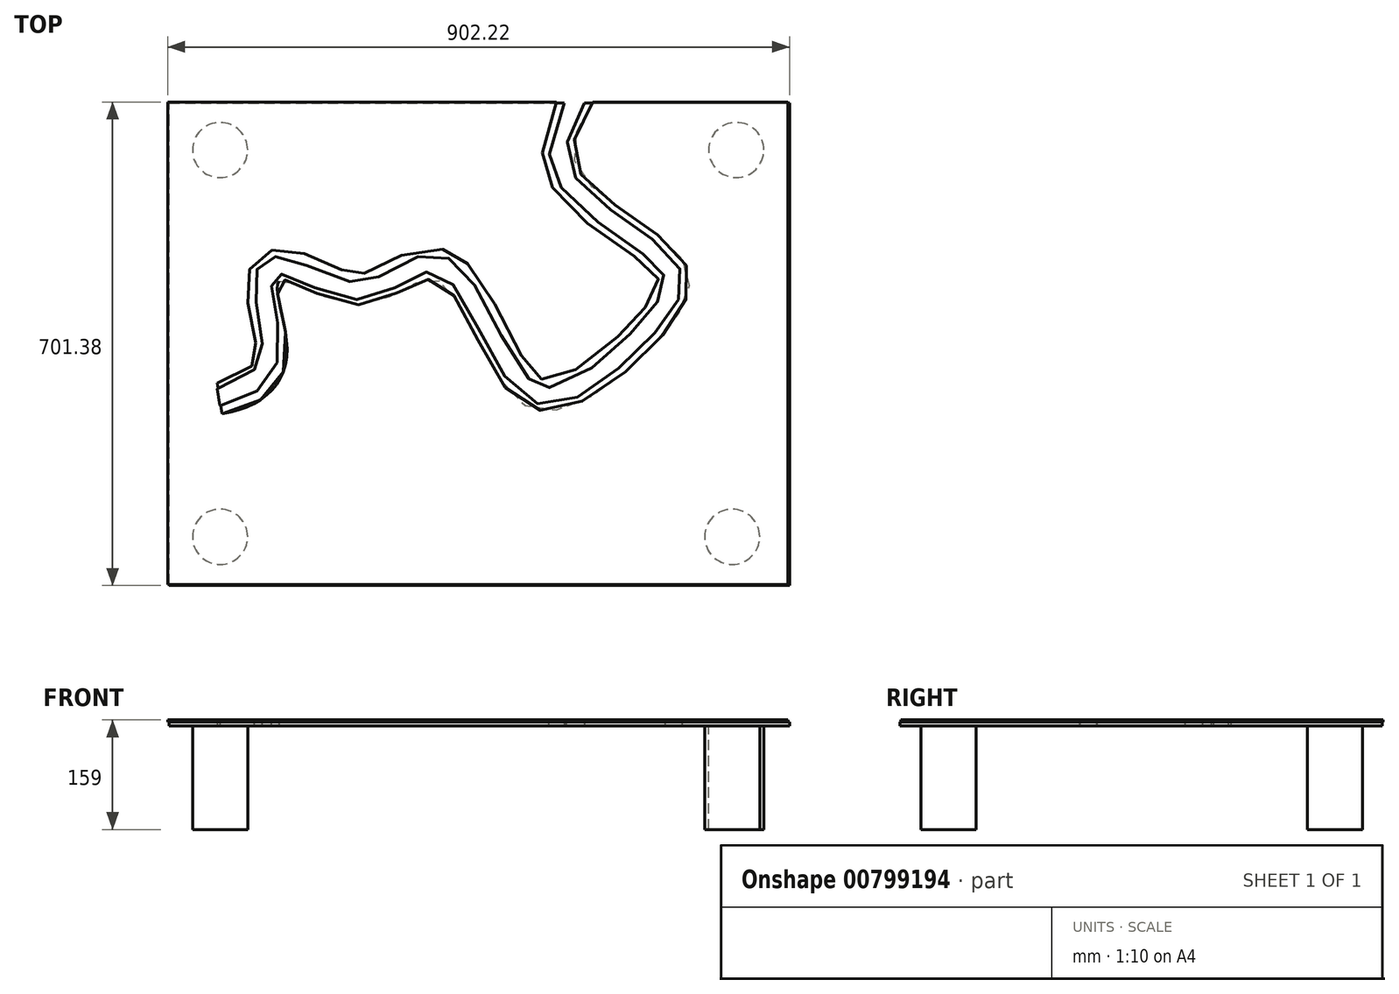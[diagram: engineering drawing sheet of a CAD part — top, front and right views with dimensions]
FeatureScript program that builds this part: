
annotation { "Feature Type Name" : "Feature", "Feature Type Description" : "" }
export const myFeature = defineFeature(function(context is Context, id is Id, definition is map)
    precondition{}
    {
        {
            var Q0;
            Q0=qCreatedBy(makeId("Top.planeOp"),FACE);
            var sketch = newSketch(context, id + "F0", { "sketchPlane" : qUnion([Q0])});
            skLineSegment(sketch, "E0.bottom", {"start": v(-313.22, -209.62) * mm, "end": v(586.78, -209.62) * mm});
            skLineSegment(sketch, "E0.top", {"start": v(-313.22, 490.38) * mm, "end": v(586.78, 490.38) * mm});
            skLineSegment(sketch, "E0.left", {"start": v(-313.22, -209.62) * mm, "end": v(-313.22, 490.38) * mm});
            skLineSegment(sketch, "E0.right", {"start": v(586.78, -209.62) * mm, "end": v(586.78, 490.38) * mm});
            skSolve(sketch);
        }
        {
            var Q0;
            Q0=qCreatedBy(makeId("Top.planeOp"),FACE);
            var sketch = newSketch(context, id + "F1", { "sketchPlane" : qUnion([Q0])});
            skFitSpline(sketch, "E1", {"points": [v(-234.3, 37.79) * mm, v(-140.37, 121) * mm, v(-151.1, 231.03) * mm, v(-33, 196.14) * mm, v(79.72, 231.03) * mm, v(203.18, 51.2) * mm, v(383, 129.04) * mm, v(436.68, 257.87) * mm, v(281.01, 394.76) * mm, v(345.43, 545.06) * mm], "startDerivative": vector(1524.68, 246.4) * mm, "endDerivative": vector(1140, 1409.82) * mm});
            skFitSpline(sketch, "E2.0", {"points": [v(-241.49, 82.21) * mm, v(-235.54, 83.17) * mm, v(-227.18, 85.14) * mm, v(-217.47, 88.6) * mm, v(-210.97, 91.54) * mm, v(-205.27, 94.74) * mm, v(-200.42, 98.12) * mm, v(-196.37, 101.6) * mm, v(-193.1, 105.12) * mm, v(-190.48, 108.67) * mm, v(-188.77, 111.71) * mm, v(-187.64, 114.26) * mm, v(-186.91, 116.25) * mm, v(-186.29, 118.34) * mm, v(-185.86, 120.2) * mm, v(-185.58, 121.76) * mm, v(-185.4, 122.98) * mm, v(-185.25, 124.24) * mm, v(-185.14, 125.55) * mm, v(-185.06, 127) * mm, v(-185, 129.09) * mm, v(-185.02, 131.99) * mm, v(-185.23, 135.87) * mm, v(-185.6, 140.08) * mm, v(-186.16, 144.57) * mm, v(-187.1, 150.85) * mm, v(-188.62, 159.15) * mm, v(-190.82, 169.5) * mm, v(-192.8, 178.27) * mm, v(-194.38, 185.3) * mm, v(-195.53, 190.6) * mm, v(-196.61, 195.94) * mm, v(-197.6, 201.35) * mm, v(-198.47, 206.9) * mm, v(-199.15, 212.74) * mm, v(-199.48, 218.02) * mm, v(-199.49, 222.66) * mm, v(-199.33, 226.42) * mm, v(-198.92, 230.53) * mm, v(-198.17, 235.06) * mm, v(-196.91, 240.08) * mm, v(-194.95, 245.63) * mm, v(-192.49, 250.64) * mm, v(-189.9, 254.77) * mm, v(-187.62, 257.88) * mm, v(-185, 260.93) * mm, v(-182.04, 263.87) * mm, v(-179.31, 266.15) * mm, v(-177, 267.85) * mm, v(-174.62, 269.45) * mm, v(-171.6, 271.2) * mm, v(-167.98, 272.95) * mm, v(-164.4, 274.33) * mm, v(-159.8, 275.75) * mm, v(-154.43, 276.82) * mm, v(-148.71, 277.31) * mm, v(-143.68, 277.28) * mm, v(-139.23, 276.9) * mm, v(-135.25, 276.33) * mm, v(-131.65, 275.6) * mm, v(-128.33, 274.8) * mm, v(-124.2, 273.62) * mm, v(-119.45, 272.03) * mm, v(-114.13, 270) * mm, v(-109.02, 267.87) * mm, v(-104, 265.67) * mm, v(-99.04, 263.41) * mm, v(-94.1, 261.12) * mm, v(-87.5, 258.07) * mm, v(-79.29, 254.3) * mm, v(-69.56, 250.1) * mm, v(-61.74, 247.1) * mm, v(-55.8, 245.08) * mm, v(-51.55, 243.8) * mm, v(-47.55, 242.76) * mm, v(-43.86, 241.98) * mm, v(-41.09, 241.53) * mm, v(-39.08, 241.3) * mm, v(-37.68, 241.18) * mm, v(-36.4, 241.12) * mm, v(-35.42, 241.1) * mm, v(-34.7, 241.11) * mm, v(-34.2, 241.13) * mm, v(-33.69, 241.15) * mm, v(-32.98, 241.2) * mm, v(-32.08, 241.3) * mm, v(-30.94, 241.45) * mm, v(-29.75, 241.65) * mm, v(-28.07, 242) * mm, v(-25.82, 242.56) * mm, v(-21.88, 243.8) * mm, v(-16.33, 245.98) * mm, v(-8.81, 249.56) * mm, v(-0.54, 253.95) * mm, v(8.45, 258.93) * mm, v(16.64, 263.34) * mm, v(23.76, 266.88) * mm, v(29.45, 269.5) * mm, v(35.56, 272) * mm, v(42.18, 274.31) * mm, v(49.42, 276.3) * mm, v(57.37, 277.8) * mm, v(66.05, 278.55) * mm, v(75.38, 278.28) * mm, v(83.51, 276.98) * mm, v(89.2, 275.43) * mm, v(92.44, 274.37) * mm, v(94.84, 273.49) * mm, v(96.82, 272.68) * mm, v(98.38, 271.98) * mm, v(99.93, 271.27) * mm, v(101.8, 270.35) * mm, v(104.7, 268.8) * mm, v(108.13, 266.74) * mm, v(111.95, 264.14) * mm, v(115.5, 261.43) * mm, v(119.93, 257.72) * mm, v(124.92, 252.93) * mm, v(130.25, 247.03) * mm, v(135.09, 241) * mm, v(139.55, 234.84) * mm, v(145.13, 226.49) * mm, v(151.56, 215.76) * mm, v(158.77, 202.5) * mm, v(165.68, 188.95) * mm, v(172.42, 175.3) * mm, v(179.06, 161.74) * mm, v(185.66, 148.52) * mm, v(192.24, 135.9) * mm, v(198.8, 124.17) * mm, v(205.28, 113.64) * mm, v(210.51, 106.14) * mm, v(214.49, 101.06) * mm, v(217.33, 97.75) * mm, v(219.98, 94.97) * mm, v(222.38, 92.74) * mm, v(224.11, 91.33) * mm, v(225.31, 90.46) * mm, v(226.12, 89.92) * mm, v(226.8, 89.5) * mm, v(227.47, 89.14) * mm, v(228.13, 88.82) * mm, v(229, 88.44) * mm, v(230.1, 88.05) * mm, v(231.55, 87.67) * mm, v(233.18, 87.38) * mm, v(235.06, 87.2) * mm, v(237.23, 87.16) * mm, v(240.56, 87.34) * mm, v(245.52, 88.08) * mm, v(252.68, 90) * mm, v(260.83, 93.03) * mm, v(269.76, 97.18) * mm, v(279.26, 102.4) * mm, v(289.15, 108.58) * mm, v(299.28, 115.62) * mm, v(309.5, 123.37) * mm, v(319.73, 131.71) * mm, v(329.83, 140.5) * mm, v(338.06, 148.1) * mm, v(344.5, 154.26) * mm, v(348.45, 158.13) * mm, v(351.56, 161.24) * mm, v(354.63, 164.33) * mm, v(358.35, 168.16) * mm, v(362.65, 172.7) * mm, v(368.12, 178.65) * mm, v(374.44, 185.9) * mm, v(381.12, 194.2) * mm, v(386.79, 202.03) * mm, v(391.37, 209.25) * mm, v(394.83, 215.7) * mm, v(397.17, 221.22) * mm, v(398.27, 224.9) * mm, v(398.76, 227.25) * mm, v(398.96, 228.73) * mm, v(399.03, 229.95) * mm, v(399.02, 230.95) * mm, v(398.94, 231.79) * mm, v(398.8, 232.54) * mm, v(398.6, 233.28) * mm, v(398.36, 233.97) * mm, v(398.1, 234.6) * mm, v(397.89, 235.03) * mm, v(397.7, 235.4) * mm, v(397.54, 235.68) * mm, v(397.36, 236) * mm, v(397.09, 236.45) * mm, v(396.68, 237.09) * mm, v(395.87, 238.27) * mm, v(394.57, 240) * mm, v(392.51, 242.4) * mm, v(389.14, 246) * mm, v(383.77, 251.06) * mm, v(375.75, 257.74) * mm, v(366.42, 264.84) * mm, v(356.04, 272.25) * mm, v(344.87, 279.92) * mm, v(333.15, 287.84) * mm, v(321.1, 296.03) * mm, v(308.9, 304.53) * mm, v(296.74, 313.4) * mm, v(284.8, 322.77) * mm, v(273.24, 332.8) * mm, v(264.04, 341.9) * mm, v(257.06, 349.83) * mm, v(252.04, 356.16) * mm, v(248.1, 361.8) * mm, v(245.13, 366.57) * mm, v(243, 370.28) * mm, v(241.31, 373.49) * mm, v(240.03, 376.13) * mm, v(238.81, 378.8) * mm, v(237.4, 382.16) * mm, v(235.37, 387.62) * mm, v(233.3, 394.55) * mm, v(231.55, 402.95) * mm, v(230.52, 411.32) * mm, v(230.17, 419.6) * mm, v(230.45, 427.73) * mm, v(231.56, 438.3) * mm, v(234.19, 450.95) * mm, v(238.83, 465.24) * mm, v(244.61, 478.77) * mm, v(251.28, 491.68) * mm, v(258.65, 504.13) * mm, v(266.58, 516.22) * mm, v(274.94, 528.03) * mm, v(283.61, 539.62) * mm, v(295.46, 554.84) * mm, v(304.5, 566) * mm, v(310.44, 573.35) * mm]});
            skLineSegment(sketch, "E3", {"start": v(-241.49, 82.21) * mm, "end": v(-234.3, 37.79) * mm});
            skLineSegment(sketch, "E4", {"start": v(345.43, 545.06) * mm, "end": v(310.44, 573.35) * mm});
            skSolve(sketch);
        }
        {
            var Q0;
            Q0=qSketchRegion(id+"F0",true);
            extrude(context, id + "F2", {"entities" : qUnion([Q0]), "depth" : 3 * mm, "offsetDistance" : 25 * mm});
        }
        {
            var Q0;
            Q0=qSketchRegion(id+"F1",true);
            extrude(context, id + "F3", {"entities" : qUnion([Q0]), "operationType" : NewBodyOperationType.REMOVE, "depth" : 25 * mm, "offsetDistance" : 25 * mm, "hasSecondDirection" : true, "secondDirectionOppositeDirection" : true, "secondDirectionDepth" : 25 * mm});
        }
        {
            var Q0;
            Q0=qCreatedBy(makeId("Top.planeOp"),FACE);
            var sketch = newSketch(context, id + "F4", { "sketchPlane" : qUnion([Q0])});
            skFitSpline(sketch, "E5", {"points": [v(-329.28, -233.28) * mm, v(-243.32, -152.04) * mm, v(-250.13, -43.12) * mm, v(-125.32, -79.42) * mm, v(-10.38, -40.77) * mm, v(117.48, -224.65) * mm, v(288.03, -142.03) * mm, v(335.32, -29.5) * mm, v(179.23, 110.07) * mm, v(250.45, 273.99) * mm], "startDerivative": vector(1524.68, 246.4) * mm, "endDerivative": vector(1140, 1409.82) * mm});
            skFitSpline(sketch, "E6.0", {"points": [v(-333.27, -208.6) * mm, v(-326.54, -207.51) * mm, v(-317.2, -205.24) * mm, v(-306.38, -201.13) * mm, v(-299.12, -197.57) * mm, v(-292.69, -193.58) * mm, v(-287.08, -189.2) * mm, v(-282.25, -184.47) * mm, v(-278.16, -179.38) * mm, v(-274.75, -173.88) * mm, v(-272, -167.9) * mm, v(-270.26, -162.45) * mm, v(-269.35, -158.34) * mm, v(-268.92, -155.91) * mm, v(-268.64, -154.04) * mm, v(-268.42, -152.13) * mm, v(-268.27, -150.5) * mm, v(-268.18, -149.16) * mm, v(-268.1, -147.79) * mm, v(-268.04, -146.03) * mm, v(-268, -143.84) * mm, v(-268.03, -140.83) * mm, v(-268.18, -136.9) * mm, v(-268.54, -131.97) * mm, v(-269.24, -125.18) * mm, v(-270.46, -116.36) * mm, v(-272.3, -105.55) * mm, v(-274.33, -94.74) * mm, v(-276.32, -84.13) * mm, v(-277.77, -75.54) * mm, v(-278.7, -68.8) * mm, v(-279.22, -63.78) * mm, v(-279.54, -58.73) * mm, v(-279.56, -53.56) * mm, v(-279.23, -49.02) * mm, v(-278.6, -45.13) * mm, v(-277.9, -42.06) * mm, v(-276.88, -38.81) * mm, v(-275.45, -35.39) * mm, v(-273.48, -31.84) * mm, v(-271.3, -28.87) * mm, v(-269.22, -26.58) * mm, v(-267.5, -24.94) * mm, v(-265.93, -23.67) * mm, v(-264.6, -22.72) * mm, v(-263.58, -22.04) * mm, v(-262.54, -21.4) * mm, v(-261.14, -20.62) * mm, v(-259.37, -19.76) * mm, v(-257.27, -18.92) * mm, v(-254.5, -18.02) * mm, v(-251.2, -17.3) * mm, v(-247.53, -16.9) * mm, v(-244.15, -16.83) * mm, v(-241.02, -17) * mm, v(-238.1, -17.36) * mm, v(-234.43, -18) * mm, v(-230.15, -19.07) * mm, v(-225.24, -20.6) * mm, v(-220.43, -22.37) * mm, v(-215.62, -24.3) * mm, v(-209.16, -27.07) * mm, v(-200.92, -30.82) * mm, v(-190.7, -35.56) * mm, v(-180.25, -40.28) * mm, v(-169.7, -44.71) * mm, v(-159.26, -48.6) * mm, v(-150.83, -51.16) * mm, v(-144.4, -52.7) * mm, v(-139.76, -53.6) * mm, v(-135.35, -54.2) * mm, v(-131.9, -54.46) * mm, v(-129.28, -54.53) * mm, v(-127.39, -54.5) * mm, v(-125.58, -54.4) * mm, v(-123.76, -54.24) * mm, v(-121.92, -54) * mm, v(-119.44, -53.6) * mm, v(-115.02, -52.63) * mm, v(-108.46, -50.55) * mm, v(-100.2, -47.01) * mm, v(-91.65, -42.63) * mm, v(-82.84, -37.63) * mm, v(-73.78, -32.3) * mm, v(-64.42, -26.92) * mm, v(-56.22, -22.65) * mm, v(-49.28, -19.55) * mm, v(-43.81, -17.45) * mm, v(-38.04, -15.66) * mm, v(-31.91, -14.28) * mm, v(-25.39, -13.48) * mm, v(-18.5, -13.42) * mm, v(-12.56, -14.13) * mm, v(-7.79, -15.23) * mm, v(-4.82, -16.13) * mm, v(-2.48, -16.98) * mm, v(-0.74, -17.69) * mm, v(0.97, -18.46) * mm, v(3.19, -19.54) * mm, v(5.85, -21.01) * mm, v(9.87, -23.56) * mm, v(14.5, -27.07) * mm, v(19.54, -31.66) * mm, v(24.17, -36.56) * mm, v(28.5, -41.75) * mm, v(32.61, -47.19) * mm, v(37.85, -54.76) * mm, v(44.07, -64.8) * mm, v(51.22, -77.59) * mm, v(58.2, -90.95) * mm, v(65.1, -104.67) * mm, v(71.98, -118.53) * mm, v(78.9, -132.26) * mm, v(85.86, -145.61) * mm, v(92.9, -158.3) * mm, v(100, -170.04) * mm, v(107.11, -180.53) * mm, v(112.99, -187.97) * mm, v(117.56, -193) * mm, v(120.9, -196.27) * mm, v(123.56, -198.58) * mm, v(125.61, -200.17) * mm, v(127.1, -201.23) * mm, v(128.3, -202.01) * mm, v(129.23, -202.58) * mm, v(130.14, -203.1) * mm, v(131.27, -203.7) * mm, v(132.63, -204.33) * mm, v(133.99, -204.9) * mm, v(135.82, -205.55) * mm, v(138.15, -206.2) * mm, v(141.08, -206.74) * mm, v(145.21, -207.13) * mm, v(150.9, -206.98) * mm, v(158.66, -205.64) * mm, v(167.24, -203.07) * mm, v(176.5, -199.26) * mm, v(186.27, -194.27) * mm, v(196.38, -188.2) * mm, v(206.71, -181.2) * mm, v(217.13, -173.38) * mm, v(227.54, -164.92) * mm, v(237.85, -155.95) * mm, v(247.97, -146.62) * mm, v(256.18, -138.68) * mm, v(262.58, -132.3) * mm, v(267.29, -127.51) * mm, v(271.9, -122.75) * mm, v(276.35, -118.06) * mm, v(280.64, -113.46) * mm, v(286.1, -107.43) * mm, v(292.45, -100.11) * mm, v(299.17, -91.72) * mm, v(304.9, -83.77) * mm, v(309.53, -76.35) * mm, v(313.03, -69.56) * mm, v(315.38, -63.52) * mm, v(316.45, -59.18) * mm, v(316.87, -56.11) * mm, v(316.98, -53.98) * mm, v(316.92, -51.98) * mm, v(316.69, -50.07) * mm, v(316.28, -48.17) * mm, v(315.78, -46.54) * mm, v(315.25, -45.2) * mm, v(314.8, -44.15) * mm, v(314.35, -43.25) * mm, v(313.96, -42.51) * mm, v(313.64, -41.95) * mm, v(313.3, -41.37) * mm, v(312.8, -40.57) * mm, v(312.12, -39.52) * mm, v(311.18, -38.19) * mm, v(309.78, -36.33) * mm, v(307.74, -33.87) * mm, v(304.84, -30.72) * mm, v(301.53, -27.42) * mm, v(296.58, -22.85) * mm, v(289.5, -16.9) * mm, v(279.83, -9.45) * mm, v(269.23, -1.78) * mm, v(257.93, 6.1) * mm, v(246.18, 14.16) * mm, v(234.19, 22.45) * mm, v(222.16, 30.97) * mm, v(210.3, 39.77) * mm, v(198.81, 48.92) * mm, v(187.87, 58.5) * mm, v(179.37, 66.95) * mm, v(173.05, 74.08) * mm, v(168.58, 79.64) * mm, v(164.41, 85.45) * mm, v(161.24, 90.51) * mm, v(158.9, 94.72) * mm, v(157.27, 97.96) * mm, v(155.76, 101.28) * mm, v(154.4, 104.64) * mm, v(153.17, 108.03) * mm, v(151.74, 112.58) * mm, v(149.76, 120.63) * mm, v(148.36, 132.2) * mm, v(148.77, 145.9) * mm, v(150.94, 159.27) * mm, v(154.56, 172.24) * mm, v(159.38, 184.86) * mm, v(165.2, 197.18) * mm, v(171.86, 209.28) * mm, v(181.66, 225.16) * mm, v(195.32, 244.62) * mm, v(213.03, 267.48) * mm, v(225.08, 282.37) * mm, v(231.01, 289.7) * mm]});
            skLineSegment(sketch, "E7", {"start": v(-333.27, -208.6) * mm, "end": v(-329.28, -233.28) * mm});
            skLineSegment(sketch, "E8", {"start": v(250.45, 273.99) * mm, "end": v(231.01, 289.7) * mm});
            skSolve(sketch);
        }
        {
            var Q0;
            Q0=makeQuery(id+"F2.opExtrude","SWEPT_BODY",BODY,{"disambiguationData":[OSD([sQuery(id+"F0.wireOp",EDGE,"E0.bottom"),sQuery(id+"F0.wireOp",EDGE,"E0.top"),sQuery(id+"F0.wireOp",EDGE,"E0.left"),sQuery(id+"F0.wireOp",EDGE,"E0.right")])]});
            transform(context, id + "F5", {"entities" : qUnion([Q0]), "transformType" : TransformType.TRANSLATION_3D, "dx" : -139 * mm, "dy" : -139 * mm, "dz" : 6 * mm, "makeCopy" : false});
        }
        {
            var Q0;
            Q0=qSketchRegion(id+"F4",true);
            extrude(context, id + "F6", {"entities" : qUnion([Q0]), "depth" : 25 * mm, "offsetDistance" : 25 * mm, "hasSecondDirection" : true, "secondDirectionOppositeDirection" : true, "secondDirectionDepth" : 25 * mm});
        }
        {
            var Q0;
            Q0=qCreatedBy(makeId("Top.planeOp"),FACE);
            var sketch = newSketch(context, id + "F7", { "sketchPlane" : qUnion([Q0])});
            skLineSegment(sketch, "E9.bottom", {"start": v(-450, -350) * mm, "end": v(450, -350) * mm});
            skLineSegment(sketch, "E9.top", {"start": v(-450, 350) * mm, "end": v(450, 350) * mm});
            skLineSegment(sketch, "E9.left", {"start": v(-450, -350) * mm, "end": v(-450, 350) * mm});
            skLineSegment(sketch, "E9.right", {"start": v(450, -350) * mm, "end": v(450, 350) * mm});
            skSolve(sketch);
        }
        {
            var Q0;
            Q0=makeQuery(id+"F6.opExtrude","SWEPT_BODY",BODY,{"disambiguationData":[OSD([sQuery(id+"F4.wireOp",EDGE,"E5"),sQuery(id+"F4.wireOp",EDGE,"E6.0"),sQuery(id+"F4.wireOp",EDGE,"E7"),sQuery(id+"F4.wireOp",EDGE,"E8")])]});
            transform(context, id + "F8", {"entities" : qUnion([Q0]), "transformType" : TransformType.TRANSLATION_3D, "dx" : -47 * mm, "dy" : 144 * mm, "dz" : 0 * mm, "makeCopy" : false});
        }
        {
            var Q0;
            Q0=qSketchRegion(id+"F7",true);
            extrude(context, id + "F9", {"entities" : qUnion([Q0]), "depth" : 6 * mm, "offsetDistance" : 25 * mm});
        }
        {
            var Q0;
            Q0=makeQuery(id+"F6.opExtrude","SWEPT_BODY",BODY,{"disambiguationData":[OSD([sQuery(id+"F4.wireOp",EDGE,"E5"),sQuery(id+"F4.wireOp",EDGE,"E6.0"),sQuery(id+"F4.wireOp",EDGE,"E7"),sQuery(id+"F4.wireOp",EDGE,"E8")])]});
            var Q1;
            Q1=makeQuery(id+"F2.opExtrude","SWEPT_BODY",BODY,{"disambiguationData":[OSD([sQuery(id+"F0.wireOp",EDGE,"E0.bottom"),sQuery(id+"F0.wireOp",EDGE,"E0.top"),sQuery(id+"F0.wireOp",EDGE,"E0.left"),sQuery(id+"F0.wireOp",EDGE,"E0.right")])]});
            var Q2;
            Q2=makeQuery(id+"F9.opExtrude","SWEPT_BODY",BODY,{"disambiguationData":[OSD([sQuery(id+"F7.wireOp",EDGE,"E9.bottom"),sQuery(id+"F7.wireOp",EDGE,"E9.top"),sQuery(id+"F7.wireOp",EDGE,"E9.left"),sQuery(id+"F7.wireOp",EDGE,"E9.right")])]});
            booleanBodies(context, id + "F10", {"operationType" : BooleanOperationType.SUBTRACTION, "tools" : qUnion([Q0]), "targets" : qUnion([Q1, Q2])});
        }
        {
            var Q0;
            Q0=makeQuery(id+"F9.opExtrude","CAP_FACE",FACE,{"disambiguationData":[OSD([sQuery(id+"F7.wireOp",EDGE,"E9.bottom"),sQuery(id+"F7.wireOp",EDGE,"E9.top"),sQuery(id+"F7.wireOp",EDGE,"E9.left"),sQuery(id+"F7.wireOp",EDGE,"E9.right")])],"isStart":true});
            var sketch = newSketch(context, id + "F11", { "sketchPlane" : qUnion([Q0])});
            skCircle(sketch, "E10", {"center": v(-634.2, 220.38) * mm, "radius": 40 * mm});
            skSolve(sketch);
        }
        {
            var Q0;
            Q0=makeQuery(id+"F11.imprint","IMPRINT",FACE,{"disambiguationData":[TD([[makeQuery(id+"F11.imprint","IMPRINT",EDGE,{"derivedFrom":sQuery(id+"F11.wireOp",EDGE,"E10")}),1.0]])]});
            extrude(context, id + "F12", {"entities" : qUnion([Q0]), "depth" : 150 * mm, "offsetDistance" : 25 * mm});
        }
        {
            var Q0;
            Q0=makeQuery(id+"F12.opExtrude","SWEPT_BODY",BODY,{"disambiguationData":[OSD([sQuery(id+"F11.wireOp",EDGE,"E10")])]});
            transform(context, id + "F13", {"entities" : qUnion([Q0]), "transformType" : TransformType.TRANSLATION_3D, "dx" : 258 * mm, "dy" : -59 * mm, "dz" : 0 * mm, "makeCopy" : false});
        }
        {
            var Q0;
            Q0=makeQuery(id+"F12.opExtrude","SWEPT_BODY",BODY,{"disambiguationData":[OSD([sQuery(id+"F11.wireOp",EDGE,"E10")])]});
            transform(context, id + "F14", {"entities" : qUnion([Q0]), "transformType" : TransformType.TRANSLATION_3D, "dx" : 0 * mm, "dy" : 561 * mm, "dz" : 0 * mm, "makeCopy" : true});
        }
        {
            var Q0;
            Q0=makeQuery(id+"F12.opExtrude","SWEPT_BODY",BODY,{"disambiguationData":[OSD([sQuery(id+"F11.wireOp",EDGE,"E10")])]});
            transform(context, id + "F15", {"entities" : qUnion([Q0]), "transformType" : TransformType.TRANSLATION_3D, "dx" : 743 * mm, "dy" : 0 * mm, "dz" : 0 * mm, "makeCopy" : true});
        }
        {
            var Q0;
            Q0=makeQuery(id+"F14.opPattern","COPY",BODY,{"derivedFrom":makeQuery(id+"F12.opExtrude","SWEPT_BODY",BODY,{"disambiguationData":[OSD([sQuery(id+"F11.wireOp",EDGE,"E10")])]}),"instanceName":"1"});
            transform(context, id + "F16", {"entities" : qUnion([Q0]), "transformType" : TransformType.TRANSLATION_3D, "dx" : 749 * mm, "dy" : 0 * mm, "dz" : 0 * mm, "makeCopy" : true});
        }
    });
